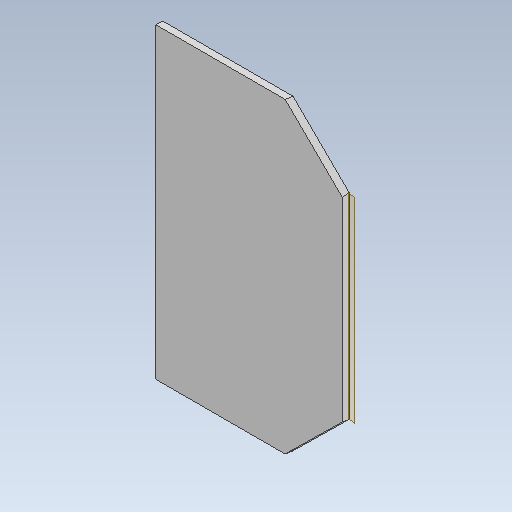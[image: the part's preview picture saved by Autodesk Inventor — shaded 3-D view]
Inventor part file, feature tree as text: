
AUTODESK INVENTOR PART (.ipt)
format: ipt  version: 2020 (Build 240168000, 168)  size: 102,912 bytes
history: native  units: mm
features: other x5, extrude x2, sketch x2
ambient origin geometry x8: Origin, YZ Plane, XZ Plane, XY Plane, X Axis, Y Axis, Z Axis, Center Point
bodies: Body1 (feature_tree)
feature tree (9):
  other  "Sólido1"
  extrude  "Extrusão1"  Depth=138.2mm TaperAngle=0.0deg
  other  "Plano de trabalho1"
  extrude  "Extrusão2"  [1 undecoded]
  sketch  "Esboço1"  dims[d0=3.0mm d1=138.2mm d2=0.0mm]
  sketch  "Esboço2"  dims[d3=13.7mm d4=0.0mm]
  other  "<userpath>\Desktop\rabo\3d\ela.iam"
  other  "ela.iam"
  other  "trás:1"
note: 1 required parameter value undecoded (feature->parameter linkage not recoverable at this tier; creation-order binding heuristic only, values carry confidence <= 0.55)
